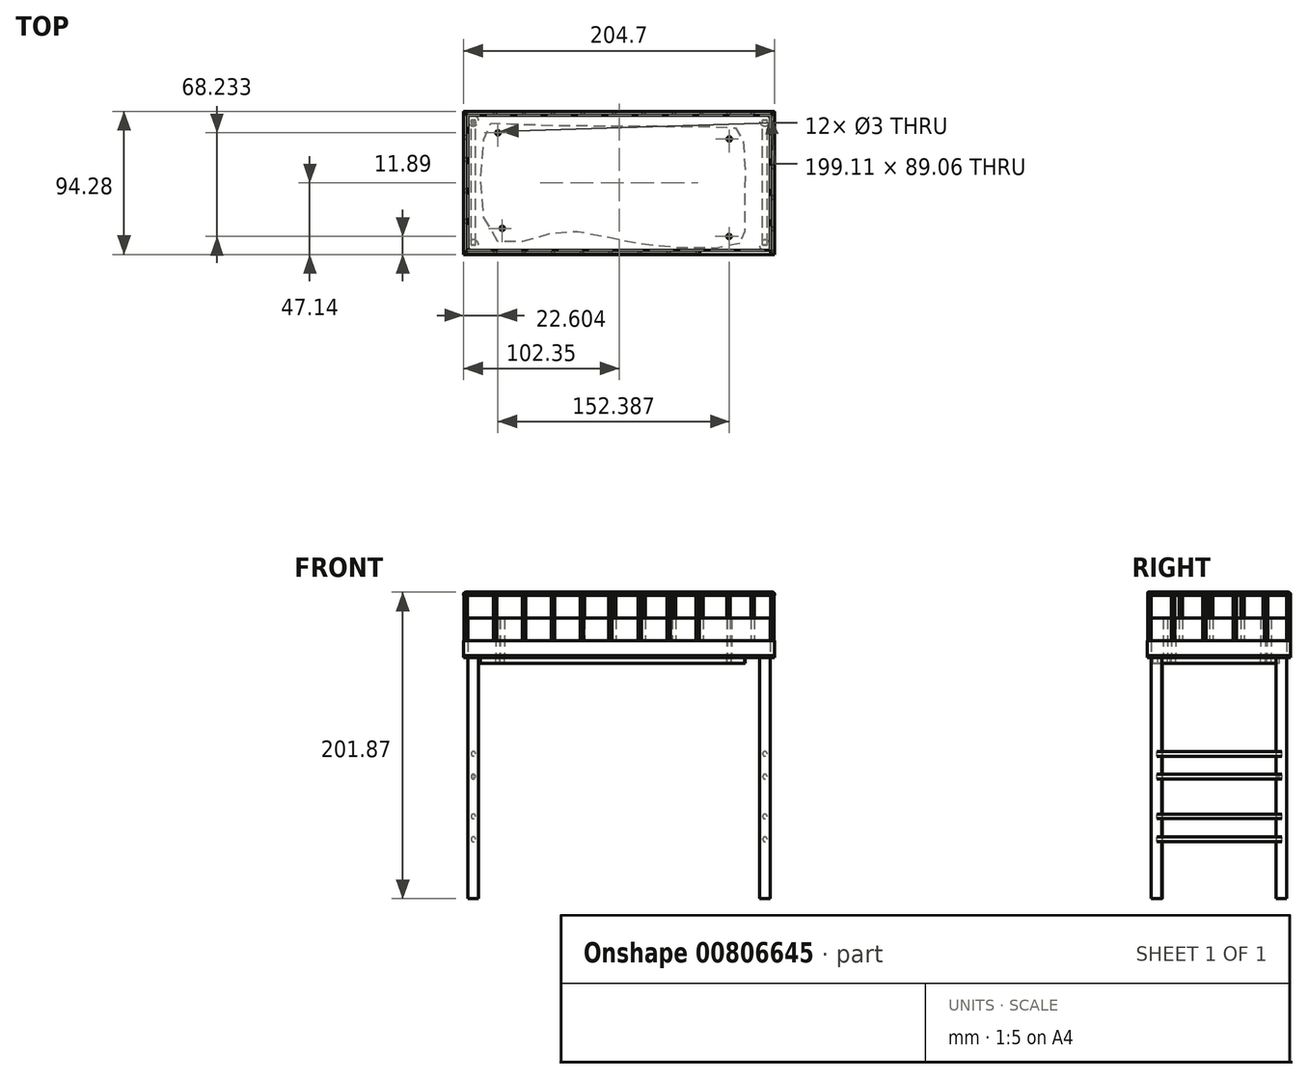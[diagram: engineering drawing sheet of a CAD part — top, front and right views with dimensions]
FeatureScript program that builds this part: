
annotation { "Feature Type Name" : "Feature", "Feature Type Description" : "" }
export const myFeature = defineFeature(function(context is Context, id is Id, definition is map)
    precondition{}
    {
        {
            var Q0;
            Q0=qCreatedBy(makeId("Top.planeOp"),FACE);
            var sketch = newSketch(context, id + "F0", { "sketchPlane" : qUnion([Q0])});
            skCircle(sketch, "E0", {"center": v(-96, 41.01) * mm, "radius": 3.5 * mm});
            skPoint(sketch, "E1.middle", {"position": v(0, 0) * mm});
            skCircle(sketch, "E2", {"center": v(96.01, 41.02) * mm, "radius": 3.5 * mm});
            skCircle(sketch, "E3", {"center": v(96.04, -41) * mm, "radius": 3.5 * mm});
            skCircle(sketch, "E4", {"center": v(-95.97, -40.92) * mm, "radius": 3.5 * mm});
            skSolve(sketch);
        }
        {
            var Q0;
            Q0=qSketchRegion(id+"F0",true);
            extrude(context, id + "F1", {"entities" : qUnion([Q0]), "depth" : 160 * mm, "offsetDistance" : 25 * mm});
        }
        {
            var Q0;
            Q0=qCreatedBy(makeId("Top.planeOp"),FACE);
            cPlane(context, id + "F2", {"entities" : qUnion([Q0]), "cplaneType" : CPlaneType.OFFSET, "offset" : 160 * mm, "width" : 150 * mm, "height" : 150 * mm});
        }
        {
            var Q0;
            Q0=qCreatedBy(id+"F2.planeOp",FACE);
            var sketch = newSketch(context, id + "F3", { "sketchPlane" : qUnion([Q0])});
            skLineSegment(sketch, "E5.bottom", {"start": v(-102.35, 47.14) * mm, "end": v(102.35, 47.14) * mm});
            skLineSegment(sketch, "E5.top", {"start": v(-102.35, -47.14) * mm, "end": v(102.35, -47.14) * mm});
            skLineSegment(sketch, "E5.left", {"start": v(-102.35, 47.14) * mm, "end": v(-102.35, -47.14) * mm});
            skLineSegment(sketch, "E5.right", {"start": v(102.35, 47.14) * mm, "end": v(102.35, -47.14) * mm});
            skPoint(sketch, "E5.middle", {"position": v(0, 0) * mm});
            skLineSegment(sketch, "E6.bottom", {"start": v(-99.56, 44.53) * mm, "end": v(99.56, 44.53) * mm});
            skLineSegment(sketch, "E6.top", {"start": v(-99.56, -44.53) * mm, "end": v(99.56, -44.53) * mm});
            skLineSegment(sketch, "E6.left", {"start": v(-99.56, 44.53) * mm, "end": v(-99.56, -44.53) * mm});
            skLineSegment(sketch, "E6.right", {"start": v(99.56, 44.53) * mm, "end": v(99.56, -44.53) * mm});
            skSolve(sketch);
        }
        {
            var Q0;
            Q0=makeQuery(id+"F3.imprint","IMPRINT",FACE,{"disambiguationData":[TD([[makeQuery(id+"F3.imprint","IMPRINT",EDGE,{"derivedFrom":sQuery(id+"F3.wireOp",EDGE,"E5.bottom")}),-1.0]])]});
            extrude(context, id + "F4", {"entities" : qUnion([Q0]), "depth" : 10 * mm, "offsetDistance" : 25 * mm});
        }
        {
            var Q0;
            Q0=makeQuery(id+"F3.imprint","IMPRINT",FACE,{"disambiguationData":[TD([[makeQuery(id+"F3.imprint","IMPRINT",EDGE,{"derivedFrom":sQuery(id+"F3.wireOp",EDGE,"E6.bottom")}),-1.0]])]});
            extrude(context, id + "F5", {"entities" : qUnion([Q0]), "depth" : 25 * mm, "offsetDistance" : 25 * mm});
        }
        {
            var Q0;
            Q0=qCreatedBy(makeId("Front.planeOp"),FACE);
            cPlane(context, id + "F6", {"entities" : qUnion([Q0]), "cplaneType" : CPlaneType.OFFSET, "offset" : 41.4 * mm, "oppositeDirection" : true, "width" : 150 * mm, "height" : 150 * mm});
        }
        {
            var Q0;
            Q0=qCreatedBy(id+"F6.planeOp",FACE);
            var sketch = newSketch(context, id + "F7", { "sketchPlane" : qUnion([Q0])});
            skCircle(sketch, "E7", {"center": v(96.06, 95.4) * mm, "radius": 1.5 * mm});
            skCircle(sketch, "E8", {"center": v(-95.9, 95.4) * mm, "radius": 1.5 * mm});
            skCircle(sketch, "E9", {"center": v(-95.9, 80.4) * mm, "radius": 1.5 * mm});
            skCircle(sketch, "E10", {"center": v(96.06, 80.4) * mm, "radius": 1.5 * mm});
            skCircle(sketch, "E11", {"center": v(96.06, 54.15) * mm, "radius": 1.5 * mm});
            skLineSegment(sketch, "E12", {"start": v(96.06, 95.4) * mm, "end": v(96.06, 80.4) * mm});
            skLineSegment(sketch, "E13", {"start": v(-95.9, 80.4) * mm, "end": v(-95.9, 95.4) * mm});
            skLineSegment(sketch, "E14", {"start": v(96.06, 54.15) * mm, "end": v(96.06, 39.15) * mm});
            skCircle(sketch, "E15", {"center": v(96.06, 39.15) * mm, "radius": 1.5 * mm});
            skCircle(sketch, "E16", {"center": v(-95.9, 54.15) * mm, "radius": 1.5 * mm});
            skCircle(sketch, "E17", {"center": v(-95.9, 39.15) * mm, "radius": 1.5 * mm});
            skSolve(sketch);
        }
        {
            var Q0;
            Q0=qSketchRegion(id+"F7",true);
            extrude(context, id + "F8", {"entities" : qUnion([Q0]), "depth" : 82.2 * mm, "offsetDistance" : 25 * mm});
        }
        {
            var Q0;
            Q0=makeQuery(id+"F5.opExtrude","CAP_EDGE",EDGE,{"disambiguationData":[OSD([sQuery(id+"F3.wireOp",EDGE,"E6.top")])],"isStart":false});
            var Q1;
            Q1=makeQuery(id+"F5.opExtrude","CAP_EDGE",EDGE,{"disambiguationData":[OSD([sQuery(id+"F3.wireOp",EDGE,"E6.left")])],"isStart":false});
            var Q2;
            Q2=makeQuery(id+"F5.opExtrude","SWEPT_EDGE",EDGE,{"disambiguationData":[OSD([sQuery(id+"F3.wireOp",EDGE,"E6.top"),sQuery(id+"F3.wireOp",EDGE,"E6.left")])]});
            var Q3;
            Q3=makeQuery(id+"F5.opExtrude","SWEPT_EDGE",EDGE,{"disambiguationData":[OSD([sQuery(id+"F3.wireOp",EDGE,"E6.bottom"),sQuery(id+"F3.wireOp",EDGE,"E6.left")])]});
            var Q4;
            Q4=makeQuery(id+"F5.opExtrude","CAP_EDGE",EDGE,{"disambiguationData":[OSD([sQuery(id+"F3.wireOp",EDGE,"E6.bottom")])],"isStart":false});
            var Q5;
            Q5=makeQuery(id+"F8.opExtrude","CAP_EDGE",EDGE,{"disambiguationData":[OSD([sQuery(id+"F7.wireOp",EDGE,"E9")])],"isStart":true});
            var Q6;
            Q6=makeQuery(id+"F8.opExtrude","CAP_FACE",FACE,{"disambiguationData":[OSD([sQuery(id+"F7.wireOp",EDGE,"E9")])],"isStart":true});
            var Q7;
            Q7=makeQuery(id+"F5.opExtrude","SWEPT_EDGE",EDGE,{"disambiguationData":[OSD([sQuery(id+"F3.wireOp",EDGE,"E6.bottom"),sQuery(id+"F3.wireOp",EDGE,"E6.right")])]});
            var Q8;
            Q8=makeQuery(id+"F5.opExtrude","CAP_FACE",FACE,{"disambiguationData":[OSD([sQuery(id+"F3.wireOp",EDGE,"E6.bottom"),sQuery(id+"F3.wireOp",EDGE,"E6.top"),sQuery(id+"F3.wireOp",EDGE,"E6.left"),sQuery(id+"F3.wireOp",EDGE,"E6.right")])],"isStart":false});
            var Q9;
            Q9=makeQuery(id+"F5.opExtrude","SWEPT_EDGE",EDGE,{"disambiguationData":[OSD([sQuery(id+"F3.wireOp",EDGE,"E6.top"),sQuery(id+"F3.wireOp",EDGE,"E6.right")])]});
            var Q10;
            Q10=makeQuery(id+"F5.opExtrude","CAP_EDGE",EDGE,{"disambiguationData":[OSD([sQuery(id+"F3.wireOp",EDGE,"E6.right")])],"isStart":false});
            fillet(context, id + "F9", {"entities" : qUnion([Q0, Q1, Q2, Q3, Q4, Q5, Q6, Q7, Q8, Q9, Q10]), "radius" : 1.42 * mm, "tangentPropagation" : true, "allowEdgeOverflow" : false});
        }
        {
            var Q0;
            Q0=makeQuery(id+"F4.opExtrude","CAP_FACE",FACE,{"disambiguationData":[OSD([sQuery(id+"F3.wireOp",EDGE,"E5.bottom"),sQuery(id+"F3.wireOp",EDGE,"E5.top"),sQuery(id+"F3.wireOp",EDGE,"E5.left"),sQuery(id+"F3.wireOp",EDGE,"E5.right"),sQuery(id+"F3.wireOp",EDGE,"E6.bottom"),sQuery(id+"F3.wireOp",EDGE,"E6.top"),sQuery(id+"F3.wireOp",EDGE,"E6.left"),sQuery(id+"F3.wireOp",EDGE,"E6.right")])],"isStart":false});
            var sketch = newSketch(context, id + "F10", { "sketchPlane" : qUnion([Q0])});
            skCircle(sketch, "E18", {"center": v(-81.67, -45.85) * mm, "radius": 1.1 * mm});
            skCircle(sketch, "E19", {"center": v(-62.7, -45.85) * mm, "radius": 1.1 * mm});
            skCircle(sketch, "E20", {"center": v(-43.53, -45.85) * mm, "radius": 1.1 * mm});
            skCircle(sketch, "E21", {"center": v(-24.57, -45.88) * mm, "radius": 1.1 * mm});
            skCircle(sketch, "E22", {"center": v(-5.66, -45.88) * mm, "radius": 1.1 * mm});
            skCircle(sketch, "E23", {"center": v(13.53, -45.88) * mm, "radius": 1.1 * mm});
            skCircle(sketch, "E24", {"center": v(32.77, -45.88) * mm, "radius": 1.1 * mm});
            skCircle(sketch, "E25", {"center": v(51.79, -45.84) * mm, "radius": 1.1 * mm});
            skCircle(sketch, "E26", {"center": v(101, -45.83) * mm, "radius": 1.1 * mm});
            skCircle(sketch, "E27", {"center": v(-81.67, 45.83) * mm, "radius": 1.1 * mm});
            skCircle(sketch, "E28", {"center": v(-62.7, 45.83) * mm, "radius": 1.1 * mm});
            skCircle(sketch, "E29", {"center": v(-43.53, 45.83) * mm, "radius": 1.1 * mm});
            skCircle(sketch, "E30", {"center": v(-23.85, 45.89) * mm, "radius": 1.1 * mm});
            skCircle(sketch, "E31", {"center": v(-3.2, 45.79) * mm, "radius": 1.1 * mm});
            skCircle(sketch, "E32", {"center": v(16.2, 45.9) * mm, "radius": 1.1 * mm});
            skCircle(sketch, "E33", {"center": v(36.12, 45.82) * mm, "radius": 1.1 * mm});
            skCircle(sketch, "E34", {"center": v(54.15, 45.82) * mm, "radius": 1.1 * mm});
            skCircle(sketch, "E35", {"center": v(72.05, 45.81) * mm, "radius": 1.1 * mm});
            skCircle(sketch, "E36", {"center": v(87.98, 45.86) * mm, "radius": 1.1 * mm});
            skCircle(sketch, "E37", {"center": v(100.93, 45.74) * mm, "radius": 1.1 * mm});
            skCircle(sketch, "E38", {"center": v(100.97, 31.05) * mm, "radius": 1.1 * mm});
            skCircle(sketch, "E39", {"center": v(101, 10.57) * mm, "radius": 1.1 * mm});
            skCircle(sketch, "E40", {"center": v(100.98, -9.62) * mm, "radius": 1.1 * mm});
            skCircle(sketch, "E41", {"center": v(100.94, -30.21) * mm, "radius": 1.1 * mm});
            skCircle(sketch, "E42", {"center": v(-101.03, 30.13) * mm, "radius": 1.1 * mm});
            skCircle(sketch, "E43", {"center": v(-101, 15.44) * mm, "radius": 1.1 * mm});
            skCircle(sketch, "E44", {"center": v(-100.96, -5.04) * mm, "radius": 1.1 * mm});
            skCircle(sketch, "E45", {"center": v(-100.99, -25.24) * mm, "radius": 1.1 * mm});
            skCircle(sketch, "E46", {"center": v(-101.03, -45.83) * mm, "radius": 1.1 * mm});
            skCircle(sketch, "E47", {"center": v(-101.03, 45.83) * mm, "radius": 1.1 * mm});
            skSolve(sketch);
        }
        {
            var Q0;
            Q0=qSketchRegion(id+"F10",true);
            extrude(context, id + "F11", {"entities" : qUnion([Q0]), "operationType" : NewBodyOperationType.ADD, "depth" : 30 * mm, "offsetDistance" : 25 * mm});
        }
        {
            var Q0;
            Q0=makeQuery(id+"F5.opExtrude","CAP_FACE",FACE,{"disambiguationData":[OSD([sQuery(id+"F3.wireOp",EDGE,"E6.bottom"),sQuery(id+"F3.wireOp",EDGE,"E6.top"),sQuery(id+"F3.wireOp",EDGE,"E6.left"),sQuery(id+"F3.wireOp",EDGE,"E6.right")])],"isStart":false});
            cPlane(context, id + "F12", {"entities" : qUnion([Q0]), "cplaneType" : CPlaneType.OFFSET, "offset" : 14.67 * mm, "width" : 150 * mm, "height" : 150 * mm});
        }
        {
            var Q0;
            Q0=qCreatedBy(id+"F12.planeOp",FACE);
            var sketch = newSketch(context, id + "F13", { "sketchPlane" : qUnion([Q0])});
            skLineSegment(sketch, "E48.bottom", {"start": v(-102.35, -47) * mm, "end": v(53.1, -47) * mm});
            skLineSegment(sketch, "E48.top", {"start": v(-102.35, 47) * mm, "end": v(102.35, 47) * mm});
            skLineSegment(sketch, "E48.left", {"start": v(-102.35, -47) * mm, "end": v(-102.35, 47) * mm});
            skLineSegment(sketch, "E48.right", {"start": v(102.35, -47) * mm, "end": v(102.35, 47) * mm});
            skPoint(sketch, "E48.middle", {"position": v(0, 0) * mm});
            skLineSegment(sketch, "E49.bottom", {"start": v(-99.85, -44.49) * mm, "end": v(53.1, -44.49) * mm});
            skLineSegment(sketch, "E49.top", {"start": v(-99.85, 44.49) * mm, "end": v(99.85, 44.49) * mm});
            skLineSegment(sketch, "E49.left", {"start": v(-99.85, -44.49) * mm, "end": v(-99.85, 44.49) * mm});
            skLineSegment(sketch, "E49.right", {"start": v(99.85, -44.49) * mm, "end": v(99.85, 44.49) * mm});
            skLineSegment(sketch, "E50", {"start": v(53.1, -47) * mm, "end": v(53.1, -44.49) * mm});
            skLineSegment(sketch, "E51", {"start": v(99.85, -44.49) * mm, "end": v(99.85, -47) * mm});
            skLineSegment(sketch, "E52", {"start": v(99.85, -47) * mm, "end": v(102.35, -47) * mm});
            skSolve(sketch);
        }
        {
            var Q0;
            Q0=makeQuery(id+"F13.imprint","IMPRINT",FACE,{"disambiguationData":[TD([[makeQuery(id+"F13.imprint","IMPRINT",EDGE,{"derivedFrom":sQuery(id+"F13.wireOp",EDGE,"E48.bottom")}),1.0]])]});
            extrude(context, id + "F14", {"entities" : qUnion([Q0]), "operationType" : NewBodyOperationType.ADD, "depth" : 2.2 * mm, "offsetDistance" : 25 * mm});
        }
        {
            var Q0;
            Q0=makeQuery(id+"F14.opExtrude","CAP_EDGE",EDGE,{"disambiguationData":[OSD([sQuery(id+"F13.wireOp",EDGE,"E48.top")])],"isStart":false});
            var Q1;
            Q1=makeQuery(id+"F14.opExtrude","CAP_EDGE",EDGE,{"disambiguationData":[OSD([sQuery(id+"F13.wireOp",EDGE,"E48.right")])],"isStart":false});
            var Q2;
            Q2=makeQuery(id+"F14.opExtrude","CAP_EDGE",EDGE,{"disambiguationData":[OSD([sQuery(id+"F13.wireOp",EDGE,"E48.bottom")])],"isStart":false});
            var Q3;
            Q3=makeQuery(id+"F14.opExtrude","CAP_EDGE",EDGE,{"disambiguationData":[OSD([sQuery(id+"F13.wireOp",EDGE,"E48.left")])],"isStart":false});
            fillet(context, id + "F15", {"entities" : qUnion([Q0, Q1, Q2, Q3]), "radius" : 1.1 * mm, "tangentPropagation" : true, "allowEdgeOverflow" : false});
        }
        {
            var Q0;
            Q0=makeQuery(id+"F14.opExtrude","CAP_EDGE",EDGE,{"disambiguationData":[OSD([sQuery(id+"F13.wireOp",EDGE,"E49.right"),sQuery(id+"F13.wireOp",EDGE,"E51")])],"isStart":false});
            var Q1;
            Q1=makeQuery(id+"F14.opExtrude","CAP_EDGE",EDGE,{"disambiguationData":[OSD([sQuery(id+"F13.wireOp",EDGE,"E49.top")])],"isStart":false});
            var Q2;
            Q2=makeQuery(id+"F14.opExtrude","CAP_EDGE",EDGE,{"disambiguationData":[OSD([sQuery(id+"F13.wireOp",EDGE,"E49.left")])],"isStart":false});
            var Q3;
            Q3=makeQuery(id+"F14.opExtrude","CAP_EDGE",EDGE,{"disambiguationData":[OSD([sQuery(id+"F13.wireOp",EDGE,"E49.bottom")])],"isStart":false});
            fillet(context, id + "F16", {"entities" : qUnion([Q0, Q1, Q2, Q3]), "radius" : 1.4 * mm, "tangentPropagation" : true, "allowEdgeOverflow" : false});
        }
        {
            var Q0;
            Q0=makeQuery(id+"F15.opFillet","BLEND_EDGE",EDGE,{"blendedFrom":[makeQuery(id+"F14.opExtrude","CAP_EDGE",EDGE,{"disambiguationData":[OSD([sQuery(id+"F13.wireOp",EDGE,"E48.right")])],"isStart":false}),makeQuery(id+"F14.opExtrude","SWEPT_FACE",FACE,{"disambiguationData":[OSD([sQuery(id+"F13.wireOp",EDGE,"E52")])]})],"blendedInto":[makeQuery(id+"F14.opExtrude","SWEPT_FACE",FACE,{"disambiguationData":[OSD([sQuery(id+"F13.wireOp",EDGE,"E52")])]})]});
            var Q1;
            Q1=makeQuery(id+"F16.opFillet","BLEND_EDGE",EDGE,{"blendedFrom":[makeQuery(id+"F14.opExtrude","CAP_EDGE",EDGE,{"disambiguationData":[OSD([sQuery(id+"F13.wireOp",EDGE,"E49.right"),sQuery(id+"F13.wireOp",EDGE,"E51")])],"isStart":false}),makeQuery(id+"F14.opExtrude","SWEPT_FACE",FACE,{"disambiguationData":[OSD([sQuery(id+"F13.wireOp",EDGE,"E52")])]})],"blendedInto":[makeQuery(id+"F14.opExtrude","SWEPT_FACE",FACE,{"disambiguationData":[OSD([sQuery(id+"F13.wireOp",EDGE,"E52")])]})]});
            var Q2;
            Q2=makeQuery(id+"F14.opExtrude","SWEPT_EDGE",EDGE,{"disambiguationData":[OSD([sQuery(id+"F13.wireOp",EDGE,"E51"),sQuery(id+"F13.wireOp",EDGE,"E52")])]});
            var Q3;
            Q3=makeQuery(id+"F14.opExtrude","CAP_EDGE",EDGE,{"disambiguationData":[OSD([sQuery(id+"F13.wireOp",EDGE,"E52")])],"isStart":true});
            var Q4;
            Q4=makeQuery(id+"F14.opExtrude","SWEPT_EDGE",EDGE,{"disambiguationData":[OSD([sQuery(id+"F13.wireOp",EDGE,"E48.right"),sQuery(id+"F13.wireOp",EDGE,"E52")])]});
            fillet(context, id + "F17", {"entities" : qUnion([Q0, Q1, Q2, Q3, Q4]), "radius" : 0.39 * mm, "tangentPropagation" : true, "allowEdgeOverflow" : false});
        }
        {
            var Q0;
            Q0=makeQuery(id+"F14.opExtrude","CAP_EDGE",EDGE,{"disambiguationData":[OSD([sQuery(id+"F13.wireOp",EDGE,"E50")])],"isStart":true});
            var Q1;
            Q1=makeQuery(id+"F15.opFillet","BLEND_EDGE",EDGE,{"blendedFrom":[makeQuery(id+"F14.opExtrude","CAP_EDGE",EDGE,{"disambiguationData":[OSD([sQuery(id+"F13.wireOp",EDGE,"E48.bottom")])],"isStart":false}),makeQuery(id+"F14.opExtrude","SWEPT_FACE",FACE,{"disambiguationData":[OSD([sQuery(id+"F13.wireOp",EDGE,"E50")])]})],"blendedInto":[makeQuery(id+"F14.opExtrude","SWEPT_FACE",FACE,{"disambiguationData":[OSD([sQuery(id+"F13.wireOp",EDGE,"E50")])]})]});
            var Q2;
            Q2=makeQuery(id+"F16.opFillet","BLEND_EDGE",EDGE,{"blendedFrom":[makeQuery(id+"F14.opExtrude","CAP_EDGE",EDGE,{"disambiguationData":[OSD([sQuery(id+"F13.wireOp",EDGE,"E49.bottom")])],"isStart":false}),makeQuery(id+"F14.opExtrude","SWEPT_FACE",FACE,{"disambiguationData":[OSD([sQuery(id+"F13.wireOp",EDGE,"E50")])]})],"blendedInto":[makeQuery(id+"F14.opExtrude","SWEPT_FACE",FACE,{"disambiguationData":[OSD([sQuery(id+"F13.wireOp",EDGE,"E50")])]})]});
            var Q3;
            Q3=makeQuery(id+"F14.opExtrude","SWEPT_EDGE",EDGE,{"disambiguationData":[OSD([sQuery(id+"F13.wireOp",EDGE,"E49.bottom"),sQuery(id+"F13.wireOp",EDGE,"E50")])]});
            var Q4;
            Q4=makeQuery(id+"F14.opExtrude","SWEPT_EDGE",EDGE,{"disambiguationData":[OSD([sQuery(id+"F13.wireOp",EDGE,"E48.bottom"),sQuery(id+"F13.wireOp",EDGE,"E50")])]});
            fillet(context, id + "F18", {"entities" : qUnion([Q0, Q1, Q2, Q3, Q4]), "radius" : 0.39 * mm, "tangentPropagation" : true, "allowEdgeOverflow" : false});
        }
        {
            var Q0;
            Q0=makeQuery(id+"F3.imprint","IMPRINT",FACE,{"disambiguationData":[TD([[makeQuery(id+"F3.imprint","IMPRINT",EDGE,{"derivedFrom":sQuery(id+"F3.wireOp",EDGE,"E6.bottom")}),-1.0]])]});
            var Q1;
            Q1=makeQuery(id+"F3.imprint","IMPRINT",FACE,{"disambiguationData":[TD([[makeQuery(id+"F3.imprint","IMPRINT",EDGE,{"derivedFrom":sQuery(id+"F3.wireOp",EDGE,"E5.bottom")}),-1.0]])]});
            extrude(context, id + "F19", {"entities" : qUnion([Q0, Q1]), "oppositeDirection" : true, "depth" : 1 * mm, "offsetDistance" : 25 * mm});
        }
        {
            var Q0;
            Q0=makeQuery(id+"F19.opExtrude","CAP_FACE",FACE,{"disambiguationData":[OSD([sQuery(id+"F3.wireOp",EDGE,"E5.bottom"),sQuery(id+"F3.wireOp",EDGE,"E5.top"),sQuery(id+"F3.wireOp",EDGE,"E5.left"),sQuery(id+"F3.wireOp",EDGE,"E5.right")])],"isStart":false});
            var sketch = newSketch(context, id + "F20", { "sketchPlane" : qUnion([Q0])});
            skFitSpline(sketch, "E53", {"points": [v(79.49, 39.87) * mm, v(8.18, 39.3) * mm, v(-42.29, 32.78) * mm, v(-82.96, 36.14) * mm, v(-87.09, -35.9) * mm, v(-75.94, -39.24) * mm, v(65.46, -37.2) * mm, v(81.17, -30.7) * mm, v(82.54, 26.71) * mm, v(79.49, 39.87) * mm]});
            skCircle(sketch, "E54", {"center": v(-76.93, 29.94) * mm, "radius": 1.5 * mm});
            skCircle(sketch, "E55", {"center": v(72.42, 35.25) * mm, "radius": 1.5 * mm});
            skCircle(sketch, "E56", {"center": v(72.64, -28.98) * mm, "radius": 1.5 * mm});
            skCircle(sketch, "E57", {"center": v(-79.75, -32.98) * mm, "radius": 1.5 * mm});
            skSolve(sketch);
        }
        {
            var Q0;
            Q0=makeQuery(id+"F20.imprint","IMPRINT",FACE,{"disambiguationData":[TD([[makeQuery(id+"F20.imprint","IMPRINT",EDGE,{"derivedFrom":sQuery(id+"F20.wireOp",EDGE,"E53")}),1.0]])]});
            extrude(context, id + "F21", {"entities" : qUnion([Q0]), "depth" : 4 * mm, "offsetDistance" : 25 * mm});
        }
        {
            var Q0;
            Q0=makeQuery(id+"F20.imprint","IMPRINT",FACE,{"disambiguationData":[TD([[makeQuery(id+"F20.imprint","IMPRINT",EDGE,{"derivedFrom":sQuery(id+"F20.wireOp",EDGE,"E54")}),1.0]])]});
            var Q1;
            Q1=makeQuery(id+"F20.imprint","IMPRINT",FACE,{"disambiguationData":[TD([[makeQuery(id+"F20.imprint","IMPRINT",EDGE,{"derivedFrom":sQuery(id+"F20.wireOp",EDGE,"E57")}),1.0]])]});
            var Q2;
            Q2=makeQuery(id+"F20.imprint","IMPRINT",FACE,{"disambiguationData":[TD([[makeQuery(id+"F20.imprint","IMPRINT",EDGE,{"derivedFrom":sQuery(id+"F20.wireOp",EDGE,"E56")}),1.0]])]});
            var Q3;
            Q3=makeQuery(id+"F20.imprint","IMPRINT",FACE,{"disambiguationData":[TD([[makeQuery(id+"F20.imprint","IMPRINT",EDGE,{"derivedFrom":sQuery(id+"F20.wireOp",EDGE,"E55")}),1.0]])]});
            extrude(context, id + "F22", {"entities" : qUnion([Q0, Q1, Q2, Q3]), "operationType" : NewBodyOperationType.REMOVE, "oppositeDirection" : true, "depth" : 46.1 * mm, "offsetDistance" : 25 * mm});
        }
    });
